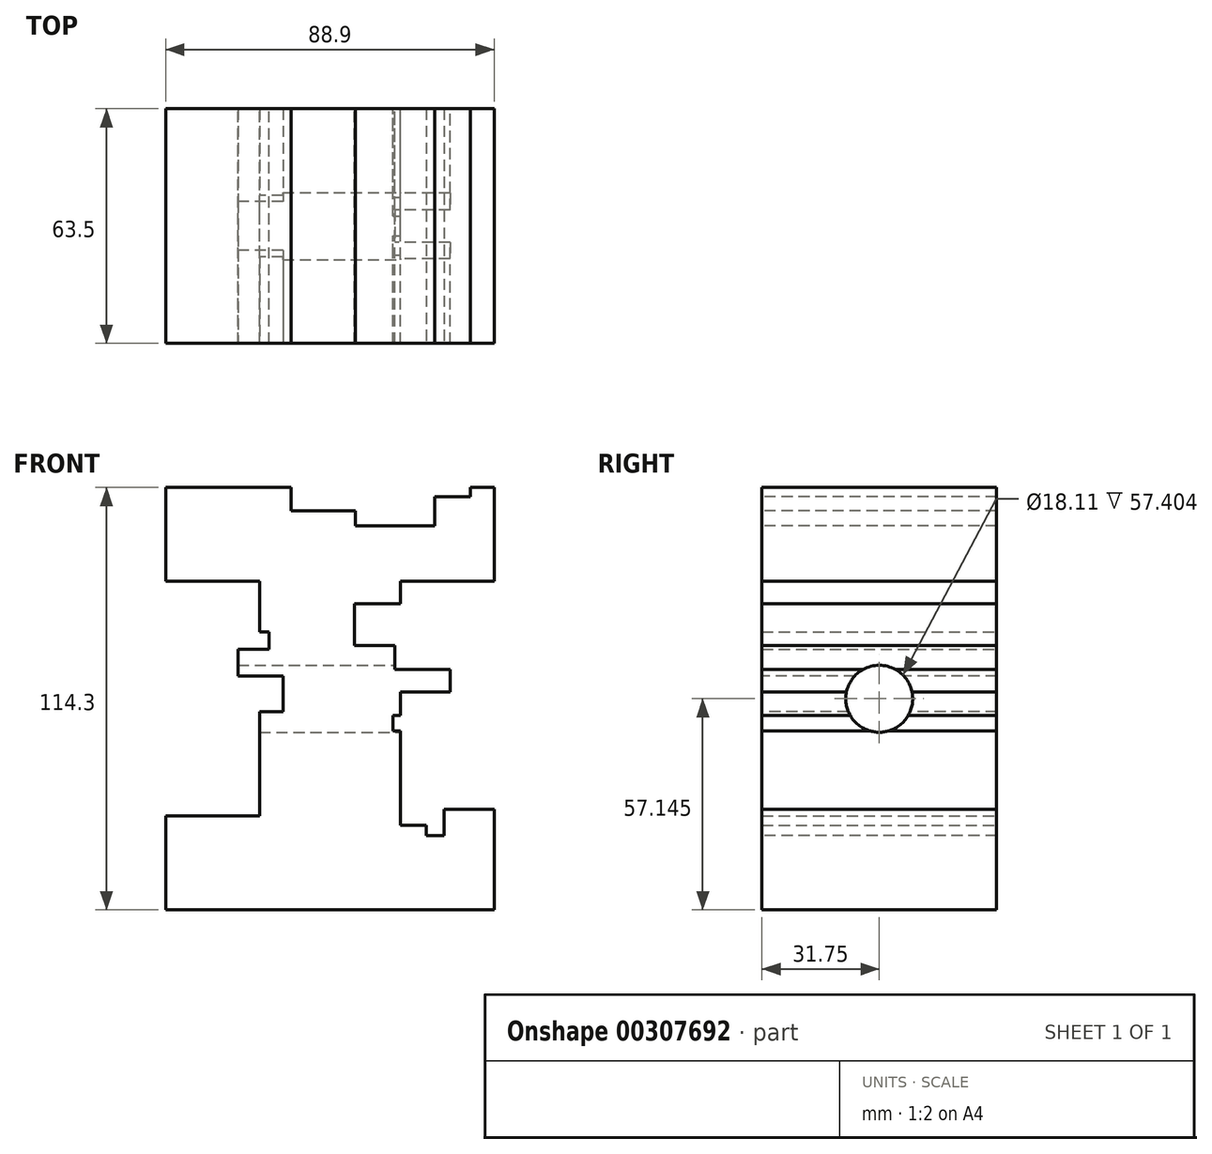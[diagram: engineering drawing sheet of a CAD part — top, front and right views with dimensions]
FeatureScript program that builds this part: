
annotation { "Feature Type Name" : "Feature", "Feature Type Description" : "" }
export const myFeature = defineFeature(function(context is Context, id is Id, definition is map)
    precondition{}
    {
        {
            var Q0;
            Q0=qCreatedBy(makeId("Front.planeOp"),FACE);
            var sketch = newSketch(context, id + "F0", { "sketchPlane" : qUnion([Q0])});
            skLineSegment(sketch, "E0", {"start": v(-43, -55.34) * mm, "end": v(45.9, -55.34) * mm});
            skLineSegment(sketch, "E1", {"start": v(45.9, -55.34) * mm, "end": v(45.9, -29.94) * mm});
            skLineSegment(sketch, "E2", {"start": v(45.9, -29.94) * mm, "end": v(20.5, -29.94) * mm});
            skLineSegment(sketch, "E3", {"start": v(20.5, -29.94) * mm, "end": v(20.5, 33.56) * mm});
            skLineSegment(sketch, "E4", {"start": v(20.5, 33.56) * mm, "end": v(45.9, 33.56) * mm});
            skLineSegment(sketch, "E5", {"start": v(45.9, 33.56) * mm, "end": v(45.9, 58.96) * mm});
            skLineSegment(sketch, "E6", {"start": v(45.9, 58.96) * mm, "end": v(-43, 58.96) * mm});
            skLineSegment(sketch, "E7", {"start": v(-43, 58.96) * mm, "end": v(-43, 33.56) * mm});
            skLineSegment(sketch, "E8", {"start": v(-43, 33.56) * mm, "end": v(-17.6, 33.56) * mm});
            skLineSegment(sketch, "E9", {"start": v(-17.6, 33.56) * mm, "end": v(-17.6, -29.94) * mm});
            skLineSegment(sketch, "E10", {"start": v(-17.6, -29.94) * mm, "end": v(-43, -29.94) * mm});
            skLineSegment(sketch, "E11", {"start": v(-43, -29.94) * mm, "end": v(-43, -55.34) * mm});
            skSolve(sketch);
        }
        {
            var Q0;
            Q0=makeQuery(id+"F0.imprint","IMPRINT",FACE,{"disambiguationData":[TD([[makeQuery(id+"F0.imprint","IMPRINT",EDGE,{"derivedFrom":sQuery(id+"F0.wireOp",EDGE,"E0")}),1.0]])]});
            extrude(context, id + "F1", {"entities" : qUnion([Q0]), "depth" : 63.5 * mm});
        }
        {
            var Q0;
            Q0=makeQuery(id+"F1.opExtrude","SWEPT_FACE",FACE,{"disambiguationData":[OSD([sQuery(id+"F0.wireOp",EDGE,"E3")])]});
            var sketch = newSketch(context, id + "F2", { "sketchPlane" : qUnion([Q0])});
            skCircle(sketch, "E12", {"center": v(-31.75, 1.8) * mm, "radius": 9.06 * mm});
            skPoint(sketch, "E12.centerSnap0", {"position": v(-31.75, 33.56) * mm});
            skPoint(sketch, "E12.centerSnap1", {"position": v(0, 1.8) * mm});
            skSolve(sketch);
        }
        {
            var Q0;
            Q0=makeQuery(id+"F2.imprint","IMPRINT",FACE,{"disambiguationData":[TD([[makeQuery(id+"F2.imprint","IMPRINT",EDGE,{"derivedFrom":sQuery(id+"F2.wireOp",EDGE,"E12")}),1.0]])]});
            extrude(context, id + "F3", {"entities" : qUnion([Q0]), "operationType" : NewBodyOperationType.REMOVE, "endBound" : BoundingType.THROUGH_ALL, "oppositeDirection" : true, "depth" : 35.3 * mm});
        }
        {
            var Q0;
            Q0=makeQuery(id+"F1.opExtrude","SWEPT_FACE",FACE,{"disambiguationData":[OSD([sQuery(id+"F0.wireOp",EDGE,"E6")])]});
            var sketch = newSketch(context, id + "F4", { "sketchPlane" : qUnion([Q0])});
            skLineSegment(sketch, "E13.bottom", {"start": v(-9.03, 0) * mm, "end": v(8.34, 0) * mm});
            skLineSegment(sketch, "E13.top", {"start": v(-9.03, -63.5) * mm, "end": v(8.34, -63.5) * mm});
            skLineSegment(sketch, "E13.left", {"start": v(-9.03, 0) * mm, "end": v(-9.03, -63.5) * mm});
            skLineSegment(sketch, "E13.right", {"start": v(8.34, 0) * mm, "end": v(8.34, -63.5) * mm});
            skSolve(sketch);
        }
        {
            var Q0;
            Q0=makeQuery(id+"F4.imprint","IMPRINT",FACE,{"disambiguationData":[TD([[makeQuery(id+"F4.imprint","IMPRINT",EDGE,{"derivedFrom":sQuery(id+"F4.wireOp",EDGE,"E13.bottom")}),1.0]])]});
            extrude(context, id + "F5", {"entities" : qUnion([Q0]), "operationType" : NewBodyOperationType.REMOVE, "oppositeDirection" : true, "depth" : 6.35 * mm});
        }
        {
            var Q0;
            {var subQ5=sQuery(id+"F0.wireOp",EDGE,"E6");var subQ6=sQuery(id+"F0.wireOp",EDGE,"E5");Q0=makeQuery(id+"F5.boolean.opBoolean","SPLIT",FACE,{"disambiguationData":[TD([makeQuery(id+"F1.opExtrude","SWEPT_FACE",FACE,{"disambiguationData":[OSD([subQ6])]})])],"derivedFrom":makeQuery(id+"F1.opExtrude","SWEPT_FACE",FACE,{"disambiguationData":[OSD([subQ5])]})});}
            var sketch = newSketch(context, id + "F6", { "sketchPlane" : qUnion([Q0])});
            skLineSegment(sketch, "E14.bottom", {"start": v(39.4, 0) * mm, "end": v(29.76, 0) * mm});
            skLineSegment(sketch, "E14.top", {"start": v(39.4, -63.5) * mm, "end": v(29.76, -63.5) * mm});
            skLineSegment(sketch, "E14.left", {"start": v(39.4, 0) * mm, "end": v(39.4, -63.5) * mm});
            skLineSegment(sketch, "E14.right", {"start": v(29.76, 0) * mm, "end": v(29.76, -63.5) * mm});
            skSolve(sketch);
        }
        {
            var Q0;
            Q0=makeQuery(id+"F6.imprint","IMPRINT",FACE,{"disambiguationData":[TD([[makeQuery(id+"F6.imprint","IMPRINT",EDGE,{"derivedFrom":sQuery(id+"F6.wireOp",EDGE,"E14.bottom")}),1.0]])]});
            extrude(context, id + "F7", {"entities" : qUnion([Q0]), "operationType" : NewBodyOperationType.REMOVE, "oppositeDirection" : true, "depth" : 2.54 * mm});
        }
        {
            var Q0;
            {var subQ5=sQuery(id+"F0.wireOp",EDGE,"E6");var subQ6=sQuery(id+"F0.wireOp",EDGE,"E5");var subQ13=makeQuery(id+"F5.opExtrude","SWEPT_FACE",FACE,{"disambiguationData":[OSD([sQuery(id+"F4.wireOp",EDGE,"E13.right")])]});Q0=makeQuery(id+"F7.boolean.opBoolean","SPLIT",FACE,{"disambiguationData":[TD([makeQuery(id+"F5.boolean.opBoolean","COPY",FACE,{"derivedFrom":subQ13})])],"derivedFrom":makeQuery(id+"F5.boolean.opBoolean","SPLIT",FACE,{"disambiguationData":[TD([makeQuery(id+"F1.opExtrude","SWEPT_FACE",FACE,{"disambiguationData":[OSD([subQ6])]})])],"derivedFrom":makeQuery(id+"F1.opExtrude","SWEPT_FACE",FACE,{"disambiguationData":[OSD([subQ5])]})})});}
            extrude(context, id + "F8", {"entities" : qUnion([Q0]), "operationType" : NewBodyOperationType.REMOVE, "oppositeDirection" : true, "depth" : 10.34 * mm});
        }
        {
            var Q0;
            Q0=makeQuery(id+"F1.opExtrude","SWEPT_FACE",FACE,{"disambiguationData":[OSD([sQuery(id+"F0.wireOp",EDGE,"E9")])]});
            var sketch = newSketch(context, id + "F9", { "sketchPlane" : qUnion([Q0])});
            skLineSegment(sketch, "E15.bottom", {"start": v(63.5, 15.24) * mm, "end": v(0, 15.24) * mm});
            skLineSegment(sketch, "E15.top", {"start": v(63.5, 19.92) * mm, "end": v(0, 19.92) * mm});
            skLineSegment(sketch, "E15.left", {"start": v(63.5, 15.24) * mm, "end": v(63.5, 19.92) * mm});
            skLineSegment(sketch, "E15.right", {"start": v(0, 15.24) * mm, "end": v(0, 19.92) * mm});
            skLineSegment(sketch, "E16.bottom", {"start": v(0, 7.99) * mm, "end": v(63.5, 7.99) * mm});
            skLineSegment(sketch, "E16.top", {"start": v(0, -1.7) * mm, "end": v(63.5, -1.7) * mm});
            skLineSegment(sketch, "E16.left", {"start": v(0, 7.99) * mm, "end": v(0, -1.7) * mm});
            skLineSegment(sketch, "E16.right", {"start": v(63.5, 7.99) * mm, "end": v(63.5, -1.7) * mm});
            skSolve(sketch);
        }
        {
            var Q0;
            Q0=makeQuery(id+"F9.imprint","IMPRINT",FACE,{"disambiguationData":[TD([[makeQuery(id+"F9.imprint","IMPRINT",EDGE,{"derivedFrom":sQuery(id+"F9.wireOp",EDGE,"E15.bottom")}),-1.0]])]});
            extrude(context, id + "F10", {"entities" : qUnion([Q0]), "operationType" : NewBodyOperationType.REMOVE, "oppositeDirection" : true, "depth" : 2.54 * mm});
        }
        {
            var Q0;
            {var subQ0=sQuery(id+"F9.wireOp",EDGE,"E16.right");Q0=makeQuery(id+"F9.imprint","IMPRINT",FACE,{"disambiguationData":[TD([[makeQuery(id+"F9.imprint","IMPRINT",EDGE,{"derivedFrom":subQ0}),-1.0]])]});}
            extrude(context, id + "F11", {"entities" : qUnion([Q0]), "operationType" : NewBodyOperationType.REMOVE, "oppositeDirection" : true, "depth" : 6.35 * mm});
        }
        {
            var Q0;
            {var subQ0=sQuery(id+"F9.wireOp",EDGE,"E16.left");Q0=makeQuery(id+"F9.imprint","IMPRINT",FACE,{"disambiguationData":[TD([[makeQuery(id+"F9.imprint","IMPRINT",EDGE,{"derivedFrom":subQ0}),1.0]])]});}
            extrude(context, id + "F12", {"entities" : qUnion([Q0]), "operationType" : NewBodyOperationType.REMOVE, "oppositeDirection" : true, "depth" : 6.35 * mm});
        }
        {
            var Q0;
            {var subQ0=sQuery(id+"F9.wireOp",EDGE,"E15.bottom");Q0=makeQuery(id+"F9.imprint","IMPRINT",FACE,{"disambiguationData":[TD([[makeQuery(id+"F9.imprint","IMPRINT",EDGE,{"derivedFrom":subQ0}),1.0]])]});}
            extrude(context, id + "F13", {"entities" : qUnion([Q0]), "operationType" : NewBodyOperationType.ADD, "depth" : 5.84 * mm});
        }
        {
            var Q0;
            Q0=makeQuery(id+"F1.opExtrude","SWEPT_FACE",FACE,{"disambiguationData":[OSD([sQuery(id+"F0.wireOp",EDGE,"E3")])]});
            var sketch = newSketch(context, id + "F14", { "sketchPlane" : qUnion([Q0])});
            skLineSegment(sketch, "E17.bottom", {"start": v(-63.5, 27.53) * mm, "end": v(0, 27.53) * mm});
            skLineSegment(sketch, "E17.top", {"start": v(-63.5, 16.18) * mm, "end": v(0, 16.18) * mm});
            skLineSegment(sketch, "E17.left", {"start": v(-63.5, 27.53) * mm, "end": v(-63.5, 16.18) * mm});
            skLineSegment(sketch, "E17.right", {"start": v(0, 27.53) * mm, "end": v(0, 16.18) * mm});
            skLineSegment(sketch, "E18.bottom", {"start": v(-63.5, -2.75) * mm, "end": v(0, -2.75) * mm});
            skLineSegment(sketch, "E18.top", {"start": v(-63.5, -6.84) * mm, "end": v(0, -6.84) * mm});
            skLineSegment(sketch, "E18.left", {"start": v(-63.5, -2.75) * mm, "end": v(-63.5, -6.84) * mm});
            skLineSegment(sketch, "E18.right", {"start": v(0, -2.75) * mm, "end": v(0, -6.84) * mm});
            skLineSegment(sketch, "E19.bottom", {"start": v(-63.5, 9.74) * mm, "end": v(0, 9.74) * mm});
            skLineSegment(sketch, "E19.top", {"start": v(-63.5, 3.6) * mm, "end": v(0, 3.6) * mm});
            skLineSegment(sketch, "E19.left", {"start": v(-63.5, 9.74) * mm, "end": v(-63.5, 3.6) * mm});
            skLineSegment(sketch, "E19.right", {"start": v(0, 9.74) * mm, "end": v(0, 3.6) * mm});
            skSolve(sketch);
        }
        {
            var Q0;
            Q0=makeQuery(id+"F14.imprint","IMPRINT",FACE,{"disambiguationData":[TD([[makeQuery(id+"F14.imprint","IMPRINT",EDGE,{"derivedFrom":sQuery(id+"F14.wireOp",EDGE,"E17.bottom")}),-1.0]])]});
            extrude(context, id + "F15", {"entities" : qUnion([Q0]), "operationType" : NewBodyOperationType.REMOVE, "oppositeDirection" : true, "depth" : 12.37 * mm});
        }
        {
            var Q0;
            {var subQ0=sQuery(id+"F14.wireOp",EDGE,"E19.left");Q0=makeQuery(id+"F14.imprint","IMPRINT",FACE,{"disambiguationData":[TD([[makeQuery(id+"F14.imprint","IMPRINT",EDGE,{"derivedFrom":subQ0}),-1.0]])]});}
            extrude(context, id + "F16", {"entities" : qUnion([Q0]), "operationType" : NewBodyOperationType.ADD, "depth" : 13.46 * mm});
        }
        {
            var Q0;
            {var subQ0=sQuery(id+"F14.wireOp",EDGE,"E19.right");Q0=makeQuery(id+"F14.imprint","IMPRINT",FACE,{"disambiguationData":[TD([[makeQuery(id+"F14.imprint","IMPRINT",EDGE,{"derivedFrom":subQ0}),1.0]])]});}
            extrude(context, id + "F17", {"entities" : qUnion([Q0]), "operationType" : NewBodyOperationType.ADD, "depth" : 13.46 * mm});
        }
        {
            var Q0;
            {var subQ0=sQuery(id+"F14.wireOp",EDGE,"E17.top");Q0=makeQuery(id+"F14.imprint","IMPRINT",FACE,{"disambiguationData":[TD([[makeQuery(id+"F14.imprint","IMPRINT",EDGE,{"derivedFrom":subQ0}),-1.0]])]});}
            extrude(context, id + "F18", {"entities" : qUnion([Q0]), "operationType" : NewBodyOperationType.REMOVE, "oppositeDirection" : true, "depth" : 1.52 * mm});
        }
        {
            var Q0;
            {var subQ0=sQuery(id+"F14.wireOp",EDGE,"E18.left");Q0=makeQuery(id+"F14.imprint","IMPRINT",FACE,{"disambiguationData":[TD([[makeQuery(id+"F14.imprint","IMPRINT",EDGE,{"derivedFrom":subQ0}),-1.0]])]});}
            extrude(context, id + "F19", {"entities" : qUnion([Q0]), "operationType" : NewBodyOperationType.REMOVE, "oppositeDirection" : true, "depth" : 1.96 * mm});
        }
        {
            var Q0;
            {var subQ0=sQuery(id+"F14.wireOp",EDGE,"E18.right");Q0=makeQuery(id+"F14.imprint","IMPRINT",FACE,{"disambiguationData":[TD([[makeQuery(id+"F14.imprint","IMPRINT",EDGE,{"derivedFrom":subQ0}),1.0]])]});}
            extrude(context, id + "F20", {"entities" : qUnion([Q0]), "operationType" : NewBodyOperationType.REMOVE, "oppositeDirection" : true, "depth" : 1.96 * mm});
        }
        {
            var Q0;
            Q0=makeQuery(id+"F1.opExtrude","SWEPT_FACE",FACE,{"disambiguationData":[OSD([sQuery(id+"F0.wireOp",EDGE,"E2")])]});
            var sketch = newSketch(context, id + "F21", { "sketchPlane" : qUnion([Q0])});
            skLineSegment(sketch, "E20.bottom", {"start": v(27.53, 0) * mm, "end": v(32.37, 0) * mm});
            skLineSegment(sketch, "E20.top", {"start": v(27.53, -63.5) * mm, "end": v(32.37, -63.5) * mm});
            skLineSegment(sketch, "E20.left", {"start": v(27.53, 0) * mm, "end": v(27.53, -63.5) * mm});
            skLineSegment(sketch, "E20.right", {"start": v(32.37, 0) * mm, "end": v(32.37, -63.5) * mm});
            skSolve(sketch);
        }
        {
            var Q0;
            Q0 = qSketchRegion(id + "F21", true);
            extrude(context, id + "F22", {"entities" : qUnion([Q0]), "operationType" : NewBodyOperationType.REMOVE, "oppositeDirection" : true, "depth" : 5.33 * mm});
        }
        {
            var Q0;
            {var subQ0=sQuery(id+"F0.wireOp",EDGE,"E1");var subQ13=sQuery(id+"F0.wireOp",EDGE,"E2");Q0=makeQuery(id+"F22.boolean.opBoolean","SPLIT",FACE,{"disambiguationData":[TD([makeQuery(id+"F1.opExtrude","SWEPT_FACE",FACE,{"disambiguationData":[OSD([subQ0])]})])],"derivedFrom":makeQuery(id+"F1.opExtrude","SWEPT_FACE",FACE,{"disambiguationData":[OSD([subQ13])]})});}
            extrude(context, id + "F23", {"entities" : qUnion([Q0]), "operationType" : NewBodyOperationType.ADD, "depth" : 1.78 * mm});
        }
        {
            var Q0;
            {var subQ0=sQuery(id+"F0.wireOp",EDGE,"E3");var subQ12=sQuery(id+"F0.wireOp",EDGE,"E2");Q0=makeQuery(id+"F22.boolean.opBoolean","SPLIT",FACE,{"disambiguationData":[TD([makeQuery(id+"F1.opExtrude","SWEPT_FACE",FACE,{"disambiguationData":[OSD([subQ0])]})])],"derivedFrom":makeQuery(id+"F1.opExtrude","SWEPT_FACE",FACE,{"disambiguationData":[OSD([subQ12])]})});}
            extrude(context, id + "F24", {"entities" : qUnion([Q0]), "operationType" : NewBodyOperationType.REMOVE, "oppositeDirection" : true, "depth" : 2.54 * mm});
        }
    });
